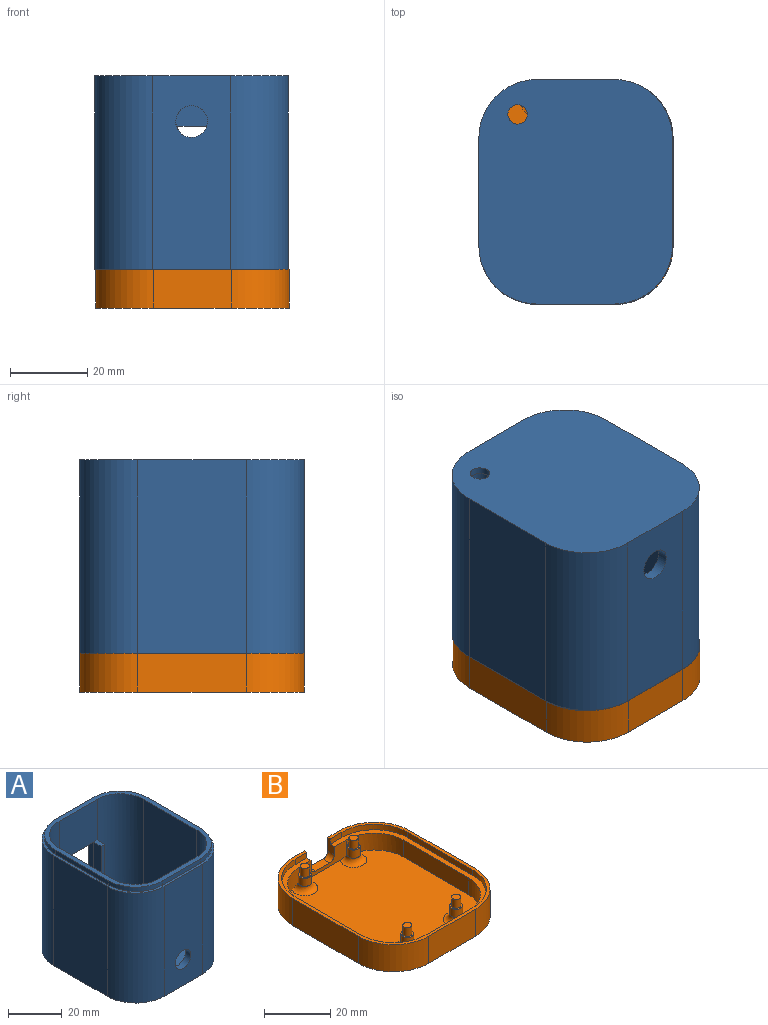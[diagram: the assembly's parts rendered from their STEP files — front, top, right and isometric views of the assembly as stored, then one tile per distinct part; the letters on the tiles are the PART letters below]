
ASSEMBLY  parts=2 mates=1
PART A: 49 faces, bbox 50x58x52 mm
  f0: plane 50.2x20mm, normal (0,-1,0), area 579.5mm2, adj f2,f23,f24,f28,f34,f35,f36,f37
  f1: plane 6x6mm, normal (0,0,1), area 8.5mm2, adj f29,f30
  f2: plane 56x48mm, normal (0,0,1), area 321mm2, adj f0,f13,f14,f15,f16,f17,f18,f19
  f3: plane 50x28mm, normal (1,0,0), area 1400mm2, adj f4,f10,f11,f12
  f4: cylinder r=15mm len=50mm, axis (0,0,-1), area 1178.1mm2, adj f3,f5,f11,f12
  f5: plane 50x20mm, normal (0,1,0), area 672mm2, adj f4,f6,f11,f12,f34,f35,f36,f37
  f6: cylinder r=15mm len=50mm, axis (0,0,-1), area 1178.1mm2, adj f5,f7,f11,f12
  f7: plane 50x28mm, normal (-1,0,0), area 1400mm2, adj f6,f8,f11,f12
  f8: cylinder r=15mm len=50mm, axis (0,0,-1), area 1178.1mm2, adj f7,f9,f11,f12
  f9: plane 50x20mm, normal (0,-1,0), area 947.2mm2, adj f8,f10,f11,f12,f48
  f10: cylinder r=15mm len=50mm, axis (0,0,-1), area 1178.1mm2, adj f3,f9,f11,f12
  f11: plane 58x50mm, normal (0,0,1), area 187.1mm2, adj f3,f4,f5,f6,f7,f8,f9,f10
  f12: plane 58x50mm, normal (0,0,-1), area 2687.1mm2, adj f3,f4,f5,f6,f7,f8,f9,f10
  f13: cylinder r=14mm len=14mm, axis (0,0,-1), area 44mm2, adj f2,f11,f19,f20
  f14: cylinder r=14mm len=14mm, axis (0,0,-1), area 44mm2, adj f2,f11,f18,f19
  f15: cylinder r=14mm len=14mm, axis (0,0,-1), area 44mm2, adj f2,f11,f17,f18
  f16: cylinder r=14mm len=14mm, axis (0,0,-1), area 44mm2, adj f2,f11,f17,f20
  f17: plane 20x2mm, normal (0,1,0), area 40mm2, adj f2,f11,f15,f16
  f18: plane 28x2mm, normal (-1,0,0), area 56mm2, adj f2,f11,f14,f15
  f19: plane 20x2mm, normal (0,-1,0), area 40mm2, adj f2,f11,f13,f14
  f20: plane 28x2mm, normal (1,0,0), area 56mm2, adj f2,f11,f13,f16
  f21: cylinder r=12.2mm len=50.2mm, axis (0,0,-1), area 962mm2, adj f2,f26,f27,f28
  f22: cylinder r=12.2mm len=50.2mm, axis (0,0,-1), area 962mm2, adj f2,f25,f26,f28
  f23: cylinder r=12.2mm len=50.2mm, axis (0,0,-1), area 962mm2, adj f0,f2,f25,f28,f40
  f24: cylinder r=12.2mm len=50.2mm, axis (0,0,-1), area 958mm2, adj f0,f2,f27,f28,f33,f44
  f25: plane 50.2x28mm, normal (1,0,0), area 1405.6mm2, adj f2,f22,f23,f28
  f26: plane 50.2x20mm, normal (0,1,0), area 951.2mm2, adj f2,f21,f22,f28,f48
  f27: plane 50.2x28mm, normal (-1,0,0), area 1405.6mm2, adj f2,f21,f24,f28
  f28: plane 52.4x44.4mm, normal (0,0,1), area 2097.4mm2, adj f0,f21,f22,f23,f24,f25,f26,f27
  f29: cylinder r=2.51mm len=5.01mm, axis (0,0,1), area 28.3mm2, adj f1,f12
  f30: cylinder r=3mm len=6mm, axis (0,0,-1), area 94.2mm2, adj f1,f32
  f31: cylinder r=4mm len=8mm, axis (0,0,-1), area 75.4mm2, adj f32,f33
  f32: plane 8x8mm, normal (0,0,1), area 22mm2, adj f30,f31
  f33: torus R=6mm, axis (0,0,1), area 80.5mm2, adj f24,f28,f31
  f34: plane 20.5x2.8mm, normal (-1,0,0), area 57.4mm2, adj f0,f5,f35,f37
  f35: plane 16x2.8mm, normal (0,0,1), area 44.8mm2, adj f0,f5,f34,f36
  f36: plane 20.5x2.8mm, normal (1,0,0), area 57.4mm2, adj f0,f5,f35,f37
  f37: plane 16x2.8mm, normal (0,0,-1), area 44.8mm2, adj f0,f5,f34,f36
  f38: plane 25.4x4mm, normal (1,0,0), area 86.9mm2, adj f0,f39,f41,f47
  f39: plane 4x1.9mm, normal (0,0,1), area 7.6mm2, adj f0,f38,f40,f41
  f40: plane 25.4x4mm, normal (-1,0,0), area 86.9mm2, adj f23,f39,f41,f47
  f41: plane 20.5x1.9mm, normal (0,-1,0), area 39mm2, adj f38,f39,f40,f47
  f42: plane 4x1.9mm, normal (0,0,1), area 7.6mm2, adj f0,f43,f44,f45
  f43: plane 25.4x4mm, normal (-1,0,0), area 86.9mm2, adj f0,f42,f45,f46
  f44: plane 25.4x4mm, normal (1,0,0), area 86.9mm2, adj f24,f42,f45,f46
  f45: plane 20.5x1.9mm, normal (0,-1,0), area 39mm2, adj f42,f43,f44,f46
  f46: cylinder r=5mm len=4.9mm, axis (1,0,0), area 13mm2, adj f0,f43,f44,f45
  f47: cylinder r=5mm len=4.9mm, axis (-1,0,0), area 13mm2, adj f0,f38,f40,f41
  f48: cylinder r=4.1mm len=8.2mm, axis (0,1,0), area 72.1mm2, adj f9,f26
PART B: 54 faces, bbox 50x58.2x10 mm
  f0: plane 52.2x44.2mm, normal (0,0,1), area 1996mm2, adj f20,f24,f25,f26,f27,f28,f29,f30
  f1: plane 5x2mm, normal (0,-1,0), area 10mm2, adj f9,f18,f32,f35
  f2: plane 28x10mm, normal (-1,0,0), area 280mm2, adj f3,f17,f18,f19
  f3: cylinder r=15mm len=15mm, axis (0,0,-1), area 235.6mm2, adj f2,f4,f18,f19
  f4: plane 20x10mm, normal (0,-1,0), area 200mm2, adj f3,f5,f18,f19
  f5: cylinder r=15mm len=15mm, axis (0,0,-1), area 235.6mm2, adj f4,f6,f18,f19
  f6: plane 28x10mm, normal (1,0,0), area 280mm2, adj f5,f7,f18,f19
  f7: cylinder r=15mm len=15mm, axis (0,0,-1), area 235.6mm2, adj f6,f8,f18,f19
  f8: plane 20x10mm, normal (0,1,0), area 131.7mm2, adj f7,f17,f18,f19,f33,f34,f35,f36
  f9: cylinder r=13.9mm len=13.9mm, axis (0,0,-1), area 43.7mm2, adj f1,f16,f18,f32
  f10: plane 5x2mm, normal (0,-1,0), area 10mm2, adj f11,f18,f32,f34
  f11: cylinder r=13.9mm len=13.9mm, axis (0,0,-1), area 43.7mm2, adj f10,f12,f18,f32
  f12: plane 28x2mm, normal (-1,0,0), area 56mm2, adj f11,f13,f18,f32
  f13: cylinder r=13.9mm len=13.9mm, axis (0,0,-1), area 43.7mm2, adj f12,f14,f18,f32
  f14: plane 20x2mm, normal (0,1,0), area 40mm2, adj f13,f15,f18,f32
  f15: cylinder r=13.9mm len=13.9mm, axis (0,0,-1), area 43.7mm2, adj f14,f16,f18,f32
  f16: plane 28x2mm, normal (1,0,0), area 56mm2, adj f9,f15,f18,f32
  f17: cylinder r=15mm len=15mm, axis (0,0,-1), area 235.6mm2, adj f2,f8,f18,f19
  f18: plane 58x50mm, normal (0,0,1), area 194.5mm2, adj f1,f2,f3,f4,f5,f6,f7,f8
  f19: plane 58x50mm, normal (0,0,-1), area 2706.9mm2, adj f2,f3,f4,f5,f6,f7,f8,f17
  f20: torus R=3.95mm, axis (0,0,1), area 47.3mm2, adj f0,f23,f24,f31
  f21: cylinder r=1.4mm len=3.2mm, axis (0,0,-1), area 28.1mm2, adj f22,f38
  f22: plane 3.9x3.9mm, normal (0,0,1), area 5.8mm2, adj f21,f23
  f23: cylinder r=1.95mm len=3.9mm, axis (0,0,-1), area 36.8mm2, adj f20,f22
  f24: cylinder r=12.1mm len=12.1mm, axis (0,0,-1), area 117mm2, adj f0,f20,f25,f31,f32
  f25: plane 28x6.2mm, normal (-1,0,0), area 173.6mm2, adj f0,f24,f26,f32
  f26: cylinder r=12.1mm len=12.1mm, axis (0,0,-1), area 117.8mm2, adj f0,f25,f27,f32
  f27: plane 20x6.2mm, normal (0,1,0), area 124mm2, adj f0,f26,f28,f32
  f28: cylinder r=12.1mm len=12.1mm, axis (0,0,-1), area 117.8mm2, adj f0,f27,f29,f32
  f29: plane 28x6.2mm, normal (1,0,0), area 173.6mm2, adj f0,f28,f30,f32
  f30: cylinder r=12.1mm len=12.1mm, axis (0,0,-1), area 117mm2, adj f0,f29,f31,f32,f52
  f31: plane 20x6.2mm, normal (0,-1,0), area 74.9mm2, adj f0,f20,f24,f30,f32,f33,f34,f35
  f32: plane 55.8x47.8mm, normal (0,0,1), area 301.8mm2, adj f1,f9,f10,f11,f12,f13,f14,f15
  f33: plane 6x2.9mm, normal (0,0,1), area 17.4mm2, adj f8,f31,f36,f37
  f34: plane 5x2.9mm, normal (-1,0,0), area 10.9mm2, adj f8,f10,f18,f31,f32,f37
  f35: plane 5x2.9mm, normal (1,0,0), area 10.9mm2, adj f1,f8,f18,f31,f32,f36
  f36: cylinder r=2mm len=2.9mm, axis (0,1,0), area 9.1mm2, adj f8,f31,f33,f35
  f37: cylinder r=2mm len=2.9mm, axis (0,-1,0), area 9.1mm2, adj f8,f31,f33,f34
  f38: plane 2.8x2.8mm, normal (0,0,1), area 6.2mm2, adj f21
  f39: plane 3.9x3.9mm, normal (0,0,1), area 5.8mm2, adj f40,f42
  f40: cylinder r=1.95mm len=3.9mm, axis (0,0,-1), area 36.8mm2, adj f39,f52
  f41: plane 2.8x2.8mm, normal (0,0,1), area 6.2mm2, adj f42
  f42: cylinder r=1.4mm len=3.2mm, axis (0,0,-1), area 28.1mm2, adj f39,f41
  f43: plane 3.9x3.9mm, normal (0,0,1), area 5.8mm2, adj f44,f46
  f44: cylinder r=1.95mm len=3.9mm, axis (0,0,-1), area 36.8mm2, adj f43,f51
  f45: plane 2.8x2.8mm, normal (0,0,1), area 6.2mm2, adj f46
  f46: cylinder r=1.4mm len=3.2mm, axis (0,0,-1), area 28.1mm2, adj f43,f45
  f47: plane 3.9x3.9mm, normal (0,0,1), area 5.8mm2, adj f48,f50
  f48: cylinder r=1.95mm len=3.9mm, axis (0,0,-1), area 36.8mm2, adj f47,f53
  f49: plane 2.8x2.8mm, normal (0,0,1), area 6.2mm2, adj f50
  f50: cylinder r=1.4mm len=3.2mm, axis (0,0,-1), area 28.1mm2, adj f47,f49
  f51: torus R=3.95mm, axis (0,0,1), area 52.8mm2, adj f0,f44
  f52: torus R=3.95mm, axis (0,0,1), area 47.3mm2, adj f0,f30,f31,f40
  f53: torus R=3.95mm, axis (0,0,1), area 52.8mm2, adj f0,f48
PLACE A rot(axis=(0,1,0),180deg) t=(-0.2,0,60)mm
PLACE B at identity fixed
MATE slider A.f7 <-> B.f6  axis (1,0,0) through (24.8,-14,10)mm
